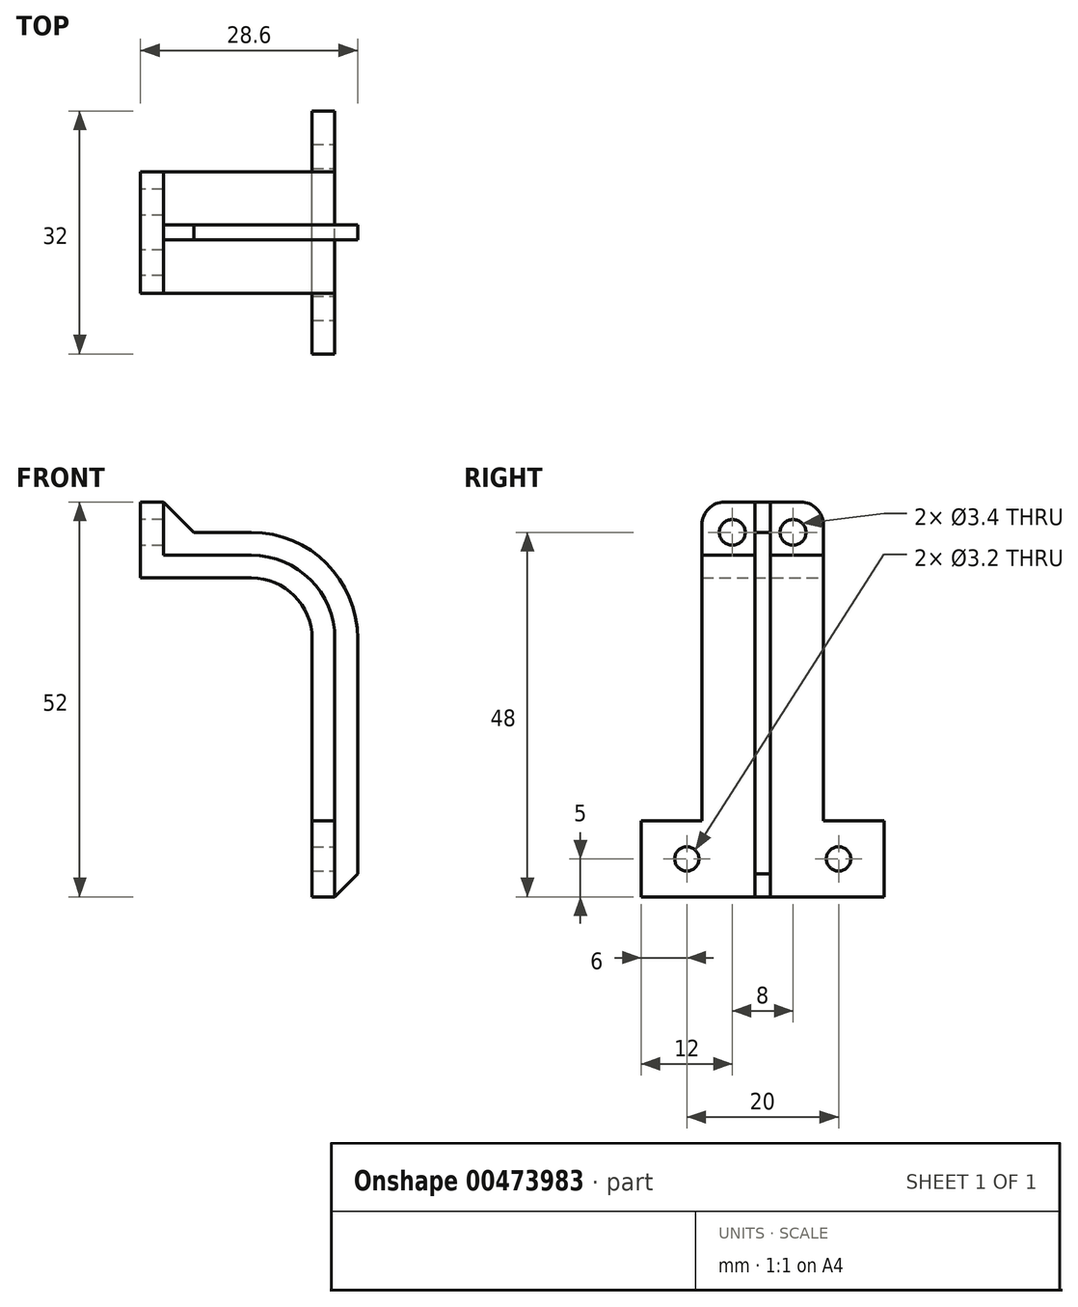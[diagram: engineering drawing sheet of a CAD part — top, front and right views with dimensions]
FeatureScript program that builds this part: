
annotation { "Feature Type Name" : "Feature", "Feature Type Description" : "" }
export const myFeature = defineFeature(function(context is Context, id is Id, definition is map)
    precondition{}
    {
        {
            var Q0;
            Q0=qCreatedBy(makeId("Front.planeOp"),FACE);
            var sketch = newSketch(context, id + "F0", { "sketchPlane" : qUnion([Q0])});
            skLineSegment(sketch, "E0", {"start": v(0, 0) * mm, "end": v(0, 34) * mm});
            skLineSegment(sketch, "E1", {"start": v(-8, 42) * mm, "end": v(-22.6, 42) * mm});
            skLineSegment(sketch, "E2", {"start": v(-19.6, 45) * mm, "end": v(-8, 45) * mm});
            skLineSegment(sketch, "E3", {"start": v(3, 34) * mm, "end": v(3, 0) * mm});
            skLineSegment(sketch, "E4", {"start": v(3, 0) * mm, "end": v(0, 0) * mm});
            skArc(sketch, "E5.filletArc", {"start": v(0, 34) * mm, "mid": v(-2.34, 39.66) * mm, "end": v(-8, 42) * mm});
            skArc(sketch, "E6", {"start": v(-8, 45) * mm, "mid": v(-0.22, 41.78) * mm, "end": v(3, 34) * mm});
            skLineSegment(sketch, "E7.top", {"start": v(-22.6, 52) * mm, "end": v(-19.6, 52) * mm});
            skLineSegment(sketch, "E7.left", {"start": v(-22.6, 42) * mm, "end": v(-22.6, 52) * mm});
            skLineSegment(sketch, "E7.right", {"start": v(-19.6, 45) * mm, "end": v(-19.6, 52) * mm});
            skSolve(sketch);
        }
        {
            var Q0;
            Q0=makeQuery(id+"F0.imprint","IMPRINT",FACE,{"disambiguationData":[TD([[makeQuery(id+"F0.imprint","IMPRINT",EDGE,{"derivedFrom":sQuery(id+"F0.wireOp",EDGE,"E0")}),-1.0]])]});
            extrude(context, id + "F1", {"entities" : qUnion([Q0]), "depth" : 8 * mm, "offsetDistance" : 25 * mm});
        }
        {
            var Q0;
            Q0=makeQuery(id+"F1.opExtrude","SWEPT_FACE",FACE,{"disambiguationData":[OSD([sQuery(id+"F0.wireOp",EDGE,"E7.left")])]});
            var sketch = newSketch(context, id + "F2", { "sketchPlane" : qUnion([Q0])});
            skCircle(sketch, "E8", {"center": v(4, 48) * mm, "radius": 1.7 * mm});
            skSolve(sketch);
        }
        {
            var Q0;
            Q0=makeQuery(id+"F2.imprint","IMPRINT",FACE,{"disambiguationData":[TD([[makeQuery(id+"F2.imprint","IMPRINT",EDGE,{"derivedFrom":sQuery(id+"F2.wireOp",EDGE,"E8")}),1.0]])]});
            extrude(context, id + "F3", {"entities" : qUnion([Q0]), "operationType" : NewBodyOperationType.REMOVE, "endBound" : BoundingType.THROUGH_ALL, "oppositeDirection" : true, "depth" : 25 * mm, "offsetDistance" : 25 * mm});
        }
        {
            var Q0;
            Q0=qCreatedBy(makeId("Front.planeOp"),FACE);
            var sketch = newSketch(context, id + "F4", { "sketchPlane" : qUnion([Q0])});
            skLineSegment(sketch, "E9", {"start": v(3, 34) * mm, "end": v(3, 0) * mm});
            skLineSegment(sketch, "E10.0", {"start": v(6, 34) * mm, "end": v(6, 3) * mm});
            skLineSegment(sketch, "E10.2", {"start": v(-15.6, 48) * mm, "end": v(-8, 48) * mm});
            skLineSegment(sketch, "E11", {"start": v(3, 0) * mm, "end": v(6, 3) * mm});
            skLineSegment(sketch, "E12", {"start": v(-19.6, 45) * mm, "end": v(-8, 45) * mm});
            skArc(sketch, "E13", {"start": v(-8, 48) * mm, "mid": v(1.9, 43.9) * mm, "end": v(6, 34) * mm});
            skArc(sketch, "E14", {"start": v(-8, 45) * mm, "mid": v(-0.22, 41.78) * mm, "end": v(3, 34) * mm});
            skLineSegment(sketch, "E15", {"start": v(-15.6, 48) * mm, "end": v(-19.6, 52) * mm});
            skLineSegment(sketch, "E16", {"start": v(-19.6, 52) * mm, "end": v(-19.6, 45) * mm});
            skSolve(sketch);
        }
        {
            var Q0;
            Q0 = qSketchRegion(id + "F4", true);
            extrude(context, id + "F5", {"entities" : qUnion([Q0]), "operationType" : NewBodyOperationType.ADD, "depth" : 1 * mm, "offsetDistance" : 25 * mm});
        }
        {
            var Q0;
            Q0=makeQuery(id+"F1.opExtrude","CAP_FACE",FACE,{"disambiguationData":[OSD([sQuery(id+"F0.wireOp",EDGE,"E0"),sQuery(id+"F0.wireOp",EDGE,"gC3CaUbp-2jlB-nbd8-JOlZ-8itRWCj0hD8E"),sQuery(id+"F0.wireOp",EDGE,"E1"),sQuery(id+"F0.wireOp",EDGE,"Qiz5auAf-SGui-mnbA-Hcoo-tOYPeqwwEZft"),sQuery(id+"F0.wireOp",EDGE,"E2"),sQuery(id+"F0.wireOp",EDGE,"3vuqX2gD-QBAg-Msn1-HA9L-RxQMxLK8fbgY"),sQuery(id+"F0.wireOp",EDGE,"E3"),sQuery(id+"F0.wireOp",EDGE,"E4")])],"isStart":false});
            var sketch = newSketch(context, id + "F6", { "sketchPlane" : qUnion([Q0])});
            skLineSegment(sketch, "E17.bottom", {"start": v(0, 0) * mm, "end": v(3, 0) * mm});
            skLineSegment(sketch, "E17.top", {"start": v(0, 10) * mm, "end": v(3, 10) * mm});
            skLineSegment(sketch, "E17.left", {"start": v(0, 0) * mm, "end": v(0, 10) * mm});
            skLineSegment(sketch, "E17.right", {"start": v(3, 0) * mm, "end": v(3, 10) * mm});
            skSolve(sketch);
        }
        {
            var Q0;
            Q0=makeQuery(id+"F6.imprint","IMPRINT",FACE,{"disambiguationData":[TD([[makeQuery(id+"F6.imprint","IMPRINT",EDGE,{"derivedFrom":sQuery(id+"F6.wireOp",EDGE,"E17.bottom")}),-1.0]])]});
            extrude(context, id + "F7", {"entities" : qUnion([Q0]), "operationType" : NewBodyOperationType.ADD, "depth" : 8 * mm, "offsetDistance" : 25 * mm});
        }
        {
            var Q0;
            Q0=makeQuery(id+"F1.opExtrude","CAP_EDGE",EDGE,{"disambiguationData":[OSD([sQuery(id+"F0.wireOp",EDGE,"E7.top")])],"isStart":false});
            fillet(context, id + "F8", {"entities" : qUnion([Q0]), "radius" : 3 * mm, "tangentPropagation" : true, "allowEdgeOverflow" : false});
        }
        {
            var Q0;
            Q0=makeQuery(id+"F7.boolean.opBoolean","MERGE",FACE,{"derivedFrom":[makeQuery(id+"F1.opExtrude","SWEPT_FACE",FACE,{"disambiguationData":[OSD([sQuery(id+"F0.wireOp",EDGE,"E3")])]}),makeQuery(id+"F7.opExtrude","SWEPT_FACE",FACE,{"disambiguationData":[OSD([sQuery(id+"F6.wireOp",EDGE,"E17.right")])]})]});
            var sketch = newSketch(context, id + "F9", { "sketchPlane" : qUnion([Q0])});
            skCircle(sketch, "E18", {"center": v(-10, 5) * mm, "radius": 1.6 * mm});
            skPoint(sketch, "E19", {"position": v(-16, 5) * mm});
            skSolve(sketch);
        }
        {
            var Q0;
            Q0=makeQuery(id+"F9.imprint","IMPRINT",FACE,{"disambiguationData":[TD([[makeQuery(id+"F9.imprint","IMPRINT",EDGE,{"derivedFrom":sQuery(id+"F9.wireOp",EDGE,"E18")}),1.0]])]});
            extrude(context, id + "F10", {"entities" : qUnion([Q0]), "operationType" : NewBodyOperationType.REMOVE, "endBound" : BoundingType.THROUGH_ALL, "oppositeDirection" : true, "depth" : 25 * mm, "offsetDistance" : 25 * mm});
        }
        {
            var Q0;
            Q0=makeQuery(id+"F1.opExtrude","SWEPT_BODY",BODY,{"disambiguationData":[OSD([sQuery(id+"F0.wireOp",EDGE,"E0"),sQuery(id+"F0.wireOp",EDGE,"gC3CaUbp-2jlB-nbd8-JOlZ-8itRWCj0hD8E"),sQuery(id+"F0.wireOp",EDGE,"E1"),sQuery(id+"F0.wireOp",EDGE,"Qiz5auAf-SGui-mnbA-Hcoo-tOYPeqwwEZft"),sQuery(id+"F0.wireOp",EDGE,"E2"),sQuery(id+"F0.wireOp",EDGE,"3vuqX2gD-QBAg-Msn1-HA9L-RxQMxLK8fbgY"),sQuery(id+"F0.wireOp",EDGE,"E3"),sQuery(id+"F0.wireOp",EDGE,"E4")])]});
            var Q1;
            Q1=qCreatedBy(makeId("Front.planeOp"),FACE);
            mirror(context, id + "F11", {"operationType" : NewBodyOperationType.ADD, "entities" : qUnion([Q0]), "mirrorPlane" : qUnion([Q1])});
        }
    });
